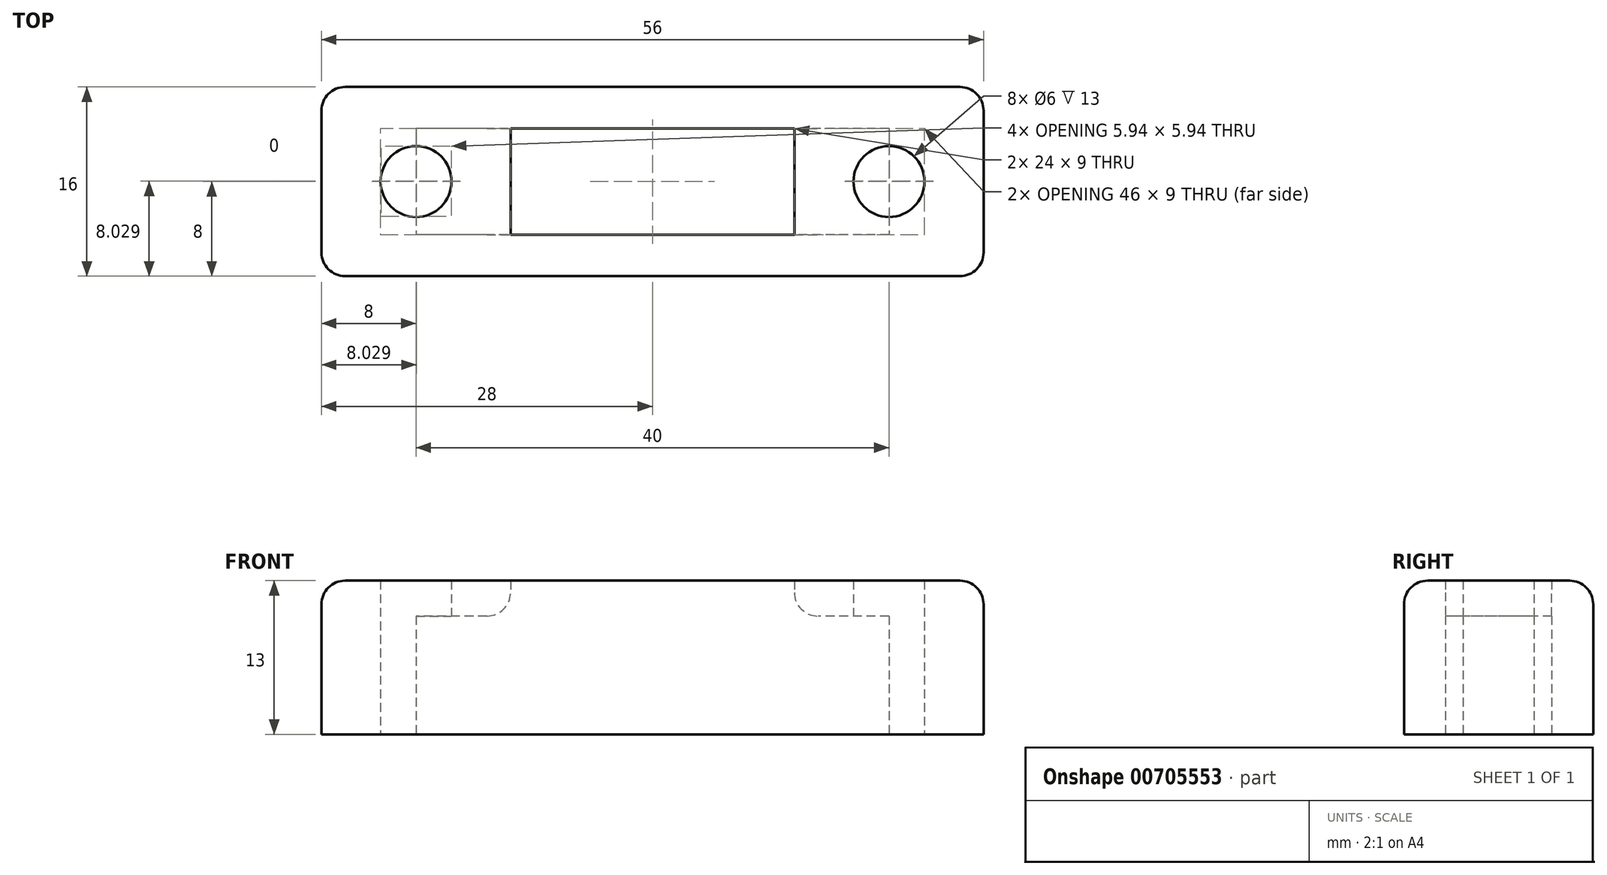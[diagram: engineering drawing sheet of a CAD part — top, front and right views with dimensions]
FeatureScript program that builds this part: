
annotation { "Feature Type Name" : "Feature", "Feature Type Description" : "" }
export const myFeature = defineFeature(function(context is Context, id is Id, definition is map)
    precondition{}
    {
        {
            var Q0;
            Q0=qCreatedBy(makeId("Top.planeOp"),FACE);
            var sketch = newSketch(context, id + "F0", { "sketchPlane" : qUnion([Q0])});
            skLineSegment(sketch, "E0.bottom", {"start": v(28, -8) * mm, "end": v(-28, -8) * mm});
            skLineSegment(sketch, "E0.top", {"start": v(28, 8) * mm, "end": v(-28, 8) * mm});
            skLineSegment(sketch, "E0.left", {"start": v(28, -8) * mm, "end": v(28, 8) * mm});
            skLineSegment(sketch, "E0.right", {"start": v(-28, -8) * mm, "end": v(-28, 8) * mm});
            skPoint(sketch, "E0.middle", {"position": v(0, 0) * mm});
            skLineSegment(sketch, "E1.bottom", {"start": v(12, -4.5) * mm, "end": v(-12, -4.5) * mm});
            skLineSegment(sketch, "E1.top", {"start": v(12, 4.5) * mm, "end": v(-12, 4.5) * mm});
            skLineSegment(sketch, "E1.left", {"start": v(12, -4.5) * mm, "end": v(12, 4.5) * mm});
            skLineSegment(sketch, "E1.right", {"start": v(-12, -4.5) * mm, "end": v(-12, 4.5) * mm});
            skLineSegment(sketch, "E2", {"start": v(-28, 0) * mm, "end": v(-20, 0) * mm});
            skCircle(sketch, "E3", {"center": v(-20, 0) * mm, "radius": 3 * mm});
            skLineSegment(sketch, "E4", {"start": v(0, 0) * mm, "end": v(0, 8) * mm});
            skCircle(sketch, "E5.MirrorC", {"center": v(20, 0) * mm, "radius": 3 * mm});
            skLineSegment(sketch, "E6.MirrorCS", {"start": v(28, 0) * mm, "end": v(20, 0) * mm});
            skSolve(sketch);
        }
        {
            var Q0;
            {var subQ8=sQuery(id+"F0.wireOp",EDGE,"E0.bottom");Q0=makeQuery(id+"F0.imprint","IMPRINT",FACE,{"disambiguationData":[TD([[makeQuery(id+"F0.imprint","IMPRINT",EDGE,{"derivedFrom":subQ8}),-1.0]])]});}
            extrude(context, id + "F1", {"entities" : qUnion([Q0]), "depth" : 13 * mm, "offsetDistance" : 25 * mm});
        }
        {
            var Q0;
            Q0=makeQuery(id+"F1.opExtrude","CAP_FACE",FACE,{"disambiguationData":[OSD([sQuery(id+"F0.wireOp",EDGE,"E0.bottom"),sQuery(id+"F0.wireOp",EDGE,"E0.top"),sQuery(id+"F0.wireOp",EDGE,"E0.left"),sQuery(id+"F0.wireOp",EDGE,"E0.right"),sQuery(id+"F0.wireOp",EDGE,"E1.bottom"),sQuery(id+"F0.wireOp",EDGE,"E1.top"),sQuery(id+"F0.wireOp",EDGE,"E1.left"),sQuery(id+"F0.wireOp",EDGE,"E1.right"),sQuery(id+"F0.wireOp",EDGE,"E3"),sQuery(id+"F0.wireOp",EDGE,"E5.MirrorC")])],"isStart":true});
            var sketch = newSketch(context, id + "F2", { "sketchPlane" : qUnion([Q0])});
            skLineSegment(sketch, "E7.bottom", {"start": v(20, -4.5) * mm, "end": v(-20, -4.5) * mm});
            skLineSegment(sketch, "E7.top", {"start": v(20, 4.5) * mm, "end": v(-20, 4.5) * mm});
            skLineSegment(sketch, "E7.left", {"start": v(20, -4.5) * mm, "end": v(20, 4.5) * mm});
            skLineSegment(sketch, "E7.right", {"start": v(-20, -4.5) * mm, "end": v(-20, 4.5) * mm});
            skPoint(sketch, "E7.middle", {"position": v(0, 0) * mm});
            skSolve(sketch);
        }
        {
            var Q0;
            Q0 = qSketchRegion(id + "F2", true);
            extrude(context, id + "F3", {"entities" : qUnion([Q0]), "operationType" : NewBodyOperationType.REMOVE, "oppositeDirection" : true, "depth" : 10 * mm, "offsetDistance" : 25 * mm});
        }
        {
            var Q0;
            Q0=makeQuery(id+"F1.opExtrude","SWEPT_EDGE",EDGE,{"disambiguationData":[OSD([sQuery(id+"F0.wireOp",EDGE,"E0.bottom"),sQuery(id+"F0.wireOp",EDGE,"E0.right")])]});
            var Q1;
            Q1=makeQuery(id+"F1.opExtrude","CAP_EDGE",EDGE,{"disambiguationData":[OSD([sQuery(id+"F0.wireOp",EDGE,"E0.bottom")])],"isStart":false});
            var Q2;
            Q2=makeQuery(id+"F1.opExtrude","CAP_EDGE",EDGE,{"disambiguationData":[OSD([sQuery(id+"F0.wireOp",EDGE,"E0.top")])],"isStart":false});
            var Q3;
            Q3=makeQuery(id+"F1.opExtrude","SWEPT_EDGE",EDGE,{"disambiguationData":[OSD([sQuery(id+"F0.wireOp",EDGE,"E0.top"),sQuery(id+"F0.wireOp",EDGE,"E0.right")])]});
            var Q4;
            Q4=makeQuery(id+"F1.opExtrude","CAP_EDGE",EDGE,{"disambiguationData":[OSD([sQuery(id+"F0.wireOp",EDGE,"E0.right")])],"isStart":false});
            var Q5;
            Q5=makeQuery(id+"F1.opExtrude","SWEPT_EDGE",EDGE,{"disambiguationData":[OSD([sQuery(id+"F0.wireOp",EDGE,"E0.top"),sQuery(id+"F0.wireOp",EDGE,"E0.left")])]});
            var Q6;
            Q6=makeQuery(id+"F1.opExtrude","CAP_EDGE",EDGE,{"disambiguationData":[OSD([sQuery(id+"F0.wireOp",EDGE,"E0.left")])],"isStart":false});
            var Q7;
            Q7=makeQuery(id+"F1.opExtrude","SWEPT_EDGE",EDGE,{"disambiguationData":[OSD([sQuery(id+"F0.wireOp",EDGE,"E0.bottom"),sQuery(id+"F0.wireOp",EDGE,"E0.left")])]});
            var Q8;
            Q8=makeQuery(id+"F3.boolean.opBoolean","INTERSECT",EDGE,{"derivedFrom":[makeQuery(id+"F1.opExtrude","SWEPT_FACE",FACE,{"disambiguationData":[OSD([sQuery(id+"F0.wireOp",EDGE,"E1.right")])]}),makeQuery(id+"F3.opExtrude","CAP_FACE",FACE,{"disambiguationData":[OSD([sQuery(id+"F2.wireOp",EDGE,"E7.bottom"),sQuery(id+"F2.wireOp",EDGE,"E7.top"),sQuery(id+"F2.wireOp",EDGE,"E7.left"),sQuery(id+"F2.wireOp",EDGE,"E7.right")])],"isStart":false})]});
            var Q9;
            Q9=makeQuery(id+"F3.boolean.opBoolean","INTERSECT",EDGE,{"derivedFrom":[makeQuery(id+"F1.opExtrude","SWEPT_FACE",FACE,{"disambiguationData":[OSD([sQuery(id+"F0.wireOp",EDGE,"E1.left")])]}),makeQuery(id+"F3.opExtrude","CAP_FACE",FACE,{"disambiguationData":[OSD([sQuery(id+"F2.wireOp",EDGE,"E7.bottom"),sQuery(id+"F2.wireOp",EDGE,"E7.top"),sQuery(id+"F2.wireOp",EDGE,"E7.left"),sQuery(id+"F2.wireOp",EDGE,"E7.right")])],"isStart":false})]});
            fillet(context, id + "F4", {"entities" : qUnion([Q0, Q1, Q2, Q3, Q4, Q5, Q6, Q7, Q8, Q9]), "radius" : 2 * mm, "tangentPropagation" : true, "allowEdgeOverflow" : false});
        }
    });
